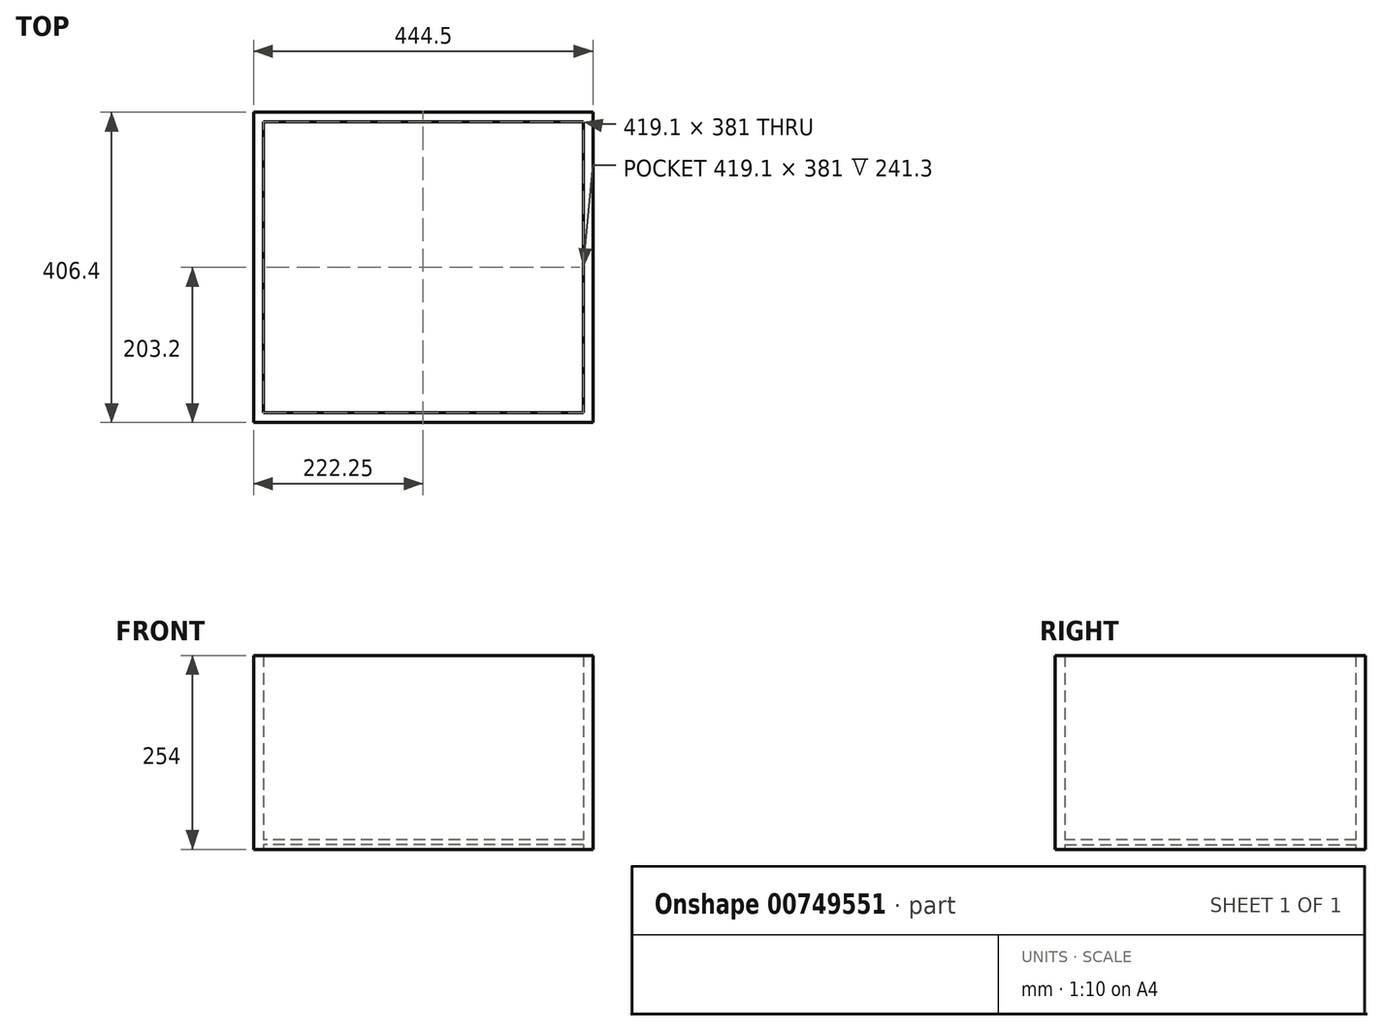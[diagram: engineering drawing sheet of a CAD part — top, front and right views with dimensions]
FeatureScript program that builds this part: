
annotation { "Feature Type Name" : "Feature", "Feature Type Description" : "" }
export const myFeature = defineFeature(function(context is Context, id is Id, definition is map)
    precondition{}
    {
        {
            var Q0;
            Q0=qCreatedBy(makeId("Top.planeOp"),FACE);
            var sketch = newSketch(context, id + "F0", { "sketchPlane" : qUnion([Q0])});
            skLineSegment(sketch, "E0.bottom", {"start": v(222.25, 203.2) * mm, "end": v(-222.25, 203.2) * mm});
            skLineSegment(sketch, "E0.top", {"start": v(222.25, -203.2) * mm, "end": v(-222.25, -203.2) * mm});
            skLineSegment(sketch, "E0.left", {"start": v(222.25, 203.2) * mm, "end": v(222.25, -203.2) * mm});
            skLineSegment(sketch, "E0.right", {"start": v(-222.25, 203.2) * mm, "end": v(-222.25, -203.2) * mm});
            skPoint(sketch, "E0.middle", {"position": v(0, 0) * mm});
            skLineSegment(sketch, "E1.bottom", {"start": v(209.55, 190.5) * mm, "end": v(-209.55, 190.5) * mm});
            skLineSegment(sketch, "E1.top", {"start": v(209.55, -190.5) * mm, "end": v(-209.55, -190.5) * mm});
            skLineSegment(sketch, "E1.left", {"start": v(209.55, 190.5) * mm, "end": v(209.55, -190.5) * mm});
            skLineSegment(sketch, "E1.right", {"start": v(-209.55, 190.5) * mm, "end": v(-209.55, -190.5) * mm});
            skSolve(sketch);
        }
        {
            var Q0;
            Q0=makeQuery(id+"F0.imprint","IMPRINT",FACE,{"disambiguationData":[TD([[makeQuery(id+"F0.imprint","IMPRINT",EDGE,{"derivedFrom":sQuery(id+"F0.wireOp",EDGE,"E0.bottom")}),1.0]])]});
            extrude(context, id + "F1", {"entities" : qUnion([Q0]), "depth" : 254 * mm, "offsetDistance" : 25.4 * mm});
        }
        {
            var Q0;
            Q0=makeQuery(id+"F1.opExtrude","CAP_FACE",FACE,{"disambiguationData":[OSD([sQuery(id+"F0.wireOp",EDGE,"E0.bottom"),sQuery(id+"F0.wireOp",EDGE,"E0.top"),sQuery(id+"F0.wireOp",EDGE,"E0.left"),sQuery(id+"F0.wireOp",EDGE,"E0.right"),sQuery(id+"F0.wireOp",EDGE,"E1.bottom"),sQuery(id+"F0.wireOp",EDGE,"E1.top"),sQuery(id+"F0.wireOp",EDGE,"E1.left"),sQuery(id+"F0.wireOp",EDGE,"E1.right")])],"isStart":true});
            var sketch = newSketch(context, id + "F2", { "sketchPlane" : qUnion([Q0])});
            skLineSegment(sketch, "E2.bottom", {"start": v(-209.55, 190.5) * mm, "end": v(209.55, 190.5) * mm});
            skLineSegment(sketch, "E2.top", {"start": v(-209.55, -190.5) * mm, "end": v(209.55, -190.5) * mm});
            skLineSegment(sketch, "E2.left", {"start": v(-209.55, 190.5) * mm, "end": v(-209.55, -190.5) * mm});
            skLineSegment(sketch, "E2.right", {"start": v(209.55, 190.5) * mm, "end": v(209.55, -190.5) * mm});
            skPoint(sketch, "E2.middle", {"position": v(0, 0) * mm});
            skSolve(sketch);
        }
        {
            var Q0;
            Q0=makeQuery(id+"F2.imprint","IMPRINT",FACE,{"disambiguationData":[TD([[makeQuery(id+"F2.imprint","IMPRINT",EDGE,{"derivedFrom":sQuery(id+"F2.wireOp",EDGE,"E2.bottom")}),1.0]])]});
            extrude(context, id + "F3", {"entities" : qUnion([Q0]), "operationType" : NewBodyOperationType.ADD, "oppositeDirection" : true, "depth" : 12.7 * mm, "offsetDistance" : 25.4 * mm});
        }
        {
            var Q0;
            Q0=makeQuery(id+"F3.boolean.opBoolean","MERGE",FACE,{"derivedFrom":[makeQuery(id+"F1.opExtrude","CAP_FACE",FACE,{"disambiguationData":[OSD([sQuery(id+"F0.wireOp",EDGE,"E0.bottom"),sQuery(id+"F0.wireOp",EDGE,"E0.top"),sQuery(id+"F0.wireOp",EDGE,"E0.left"),sQuery(id+"F0.wireOp",EDGE,"E0.right"),sQuery(id+"F0.wireOp",EDGE,"E1.bottom"),sQuery(id+"F0.wireOp",EDGE,"E1.top"),sQuery(id+"F0.wireOp",EDGE,"E1.left"),sQuery(id+"F0.wireOp",EDGE,"E1.right")])],"isStart":true}),makeQuery(id+"F3.opExtrude","CAP_FACE",FACE,{"disambiguationData":[OSD([sQuery(id+"F2.wireOp",EDGE,"E2.bottom"),sQuery(id+"F2.wireOp",EDGE,"E2.top"),sQuery(id+"F2.wireOp",EDGE,"E2.left"),sQuery(id+"F2.wireOp",EDGE,"E2.right")])],"isStart":true})]});
            var sketch = newSketch(context, id + "F4", { "sketchPlane" : qUnion([Q0])});
            skLineSegment(sketch, "E3.bottom", {"start": v(209.55, 190.5) * mm, "end": v(-209.55, 190.5) * mm});
            skLineSegment(sketch, "E3.top", {"start": v(209.55, -190.5) * mm, "end": v(-209.55, -190.5) * mm});
            skLineSegment(sketch, "E3.left", {"start": v(209.55, 190.5) * mm, "end": v(209.55, -190.5) * mm});
            skLineSegment(sketch, "E3.right", {"start": v(-209.55, 190.5) * mm, "end": v(-209.55, -190.5) * mm});
            skPoint(sketch, "E3.middle", {"position": v(0, 0) * mm});
            skSolve(sketch);
        }
        {
            var Q0;
            Q0=makeQuery(id+"F4.imprint","IMPRINT",FACE,{"disambiguationData":[TD([[makeQuery(id+"F4.imprint","IMPRINT",EDGE,{"derivedFrom":sQuery(id+"F4.wireOp",EDGE,"E3.bottom")}),1.0]])]});
            extrude(context, id + "F5", {"entities" : qUnion([Q0]), "operationType" : NewBodyOperationType.REMOVE, "oppositeDirection" : true, "depth" : 6.35 * mm, "offsetDistance" : 25.4 * mm});
        }
    });
